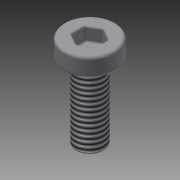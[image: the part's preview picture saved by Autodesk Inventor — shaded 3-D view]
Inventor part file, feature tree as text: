
AUTODESK INVENTOR PART (.ipt)
format: ipt  version: 2013 (Build 170138000, 138)  size: 161,280 bytes
history: native  units: mm
features: extrude x3, sketch x3, fillet x2, other x1, thread x1
ambient origin geometry x1: Origin
feature tree (10):
  other  "ソリッド1"
  extrude  "押し出し1"  Depth=5.5mm
  extrude  "押し出し2"  Depth=2.0mm TaperAngle=0.0deg
  extrude  "押し出し3"  Depth=3.0mm
  fillet  "フィレット1"  Radius=8.0mm
  fillet  "フィレット2"  Radius=1.25mm
  thread  "ねじ2"
  sketch  "スケッチ1"
  sketch  "スケッチ2"
  sketch  "スケッチ3"
